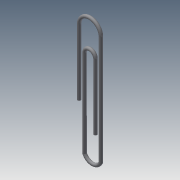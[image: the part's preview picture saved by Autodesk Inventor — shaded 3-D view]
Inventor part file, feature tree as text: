
AUTODESK INVENTOR PART (.ipt)
format: ipt  version: 2015 (Build 190159000, 159)  size: 104,960 bytes
history: native  units: in
note: dims shown in document units (in); Inventor stores cm internally (conversion verified against a paired STEP export)
features: sketch x2, plane x1, sweep x1
ambient origin geometry x8: Origin, YZ Plane, XZ Plane, XY Plane, X Axis, Y Axis, Z Axis, Center Point
bodies: Solid1 (feature_tree)
feature tree (4):
  sketch  "Sketch1"  dims[d7=0.15in d8=0.0in d9=0.0in]
  plane  "Work Plane1"
  sweep  "Sweep1"
  sketch  "Sketch2"
